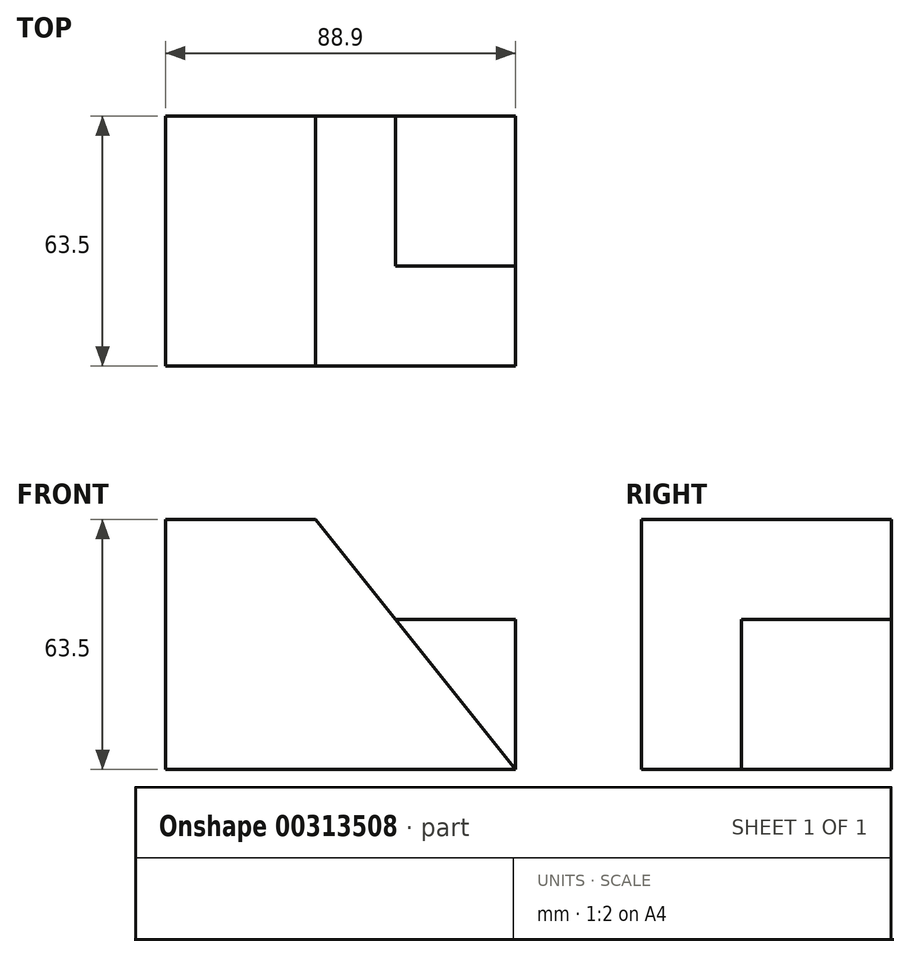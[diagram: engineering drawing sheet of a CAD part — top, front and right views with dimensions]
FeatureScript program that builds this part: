
annotation { "Feature Type Name" : "Feature", "Feature Type Description" : "" }
export const myFeature = defineFeature(function(context is Context, id is Id, definition is map)
    precondition{}
    {
        {
            var Q0;
            Q0=qCreatedBy(makeId("Front.planeOp"),FACE);
            var sketch = newSketch(context, id + "F0", { "sketchPlane" : qUnion([Q0])});
            skLineSegment(sketch, "E0", {"start": v(-58.27, -11.52) * mm, "end": v(30.63, -11.52) * mm});
            skLineSegment(sketch, "E1", {"start": v(-58.27, -11.52) * mm, "end": v(-58.27, 51.98) * mm});
            skLineSegment(sketch, "E2", {"start": v(-58.27, 51.98) * mm, "end": v(-20.17, 51.98) * mm});
            skLineSegment(sketch, "E3", {"start": v(-20.17, 51.98) * mm, "end": v(30.63, -11.52) * mm});
            skSolve(sketch);
        }
        {
            var Q0;
            Q0 = qSketchRegion(id + "F0", true);
            extrude(context, id + "F1", {"entities" : qUnion([Q0]), "depth" : 63.5 * mm});
        }
        {
            var Q0;
            Q0=makeQuery(id+"F1.opExtrude","CAP_FACE",FACE,{"disambiguationData":[OSD([sQuery(id+"F0.wireOp",EDGE,"E0"),sQuery(id+"F0.wireOp",EDGE,"E1"),sQuery(id+"F0.wireOp",EDGE,"E2"),sQuery(id+"F0.wireOp",EDGE,"E3")])],"isStart":true});
            var sketch = newSketch(context, id + "F2", { "sketchPlane" : qUnion([Q0])});
            skLineSegment(sketch, "E4", {"start": v(-30.63, -11.52) * mm, "end": v(-30.63, 26.58) * mm});
            skLineSegment(sketch, "E5", {"start": v(-30.63, 26.58) * mm, "end": v(-0.15, 26.58) * mm});
            skSolve(sketch);
        }
        {
            var Q0;
            Q0 = qSketchRegion(id + "F2", true);
            var Q1;
            {var subQ0=sQuery(id+"F2.wireOp",EDGE,"E4");Q1=makeQuery(id+"F2.imprint","IMPRINT",FACE,{"disambiguationData":[TD([[makeQuery(id+"F2.imprint","IMPRINT",EDGE,{"derivedFrom":subQ0}),-1.0]])]});}
            extrude(context, id + "F3", {"entities" : qUnion([Q0, Q1]), "operationType" : NewBodyOperationType.ADD, "oppositeDirection" : true, "depth" : 38.1 * mm});
        }
    });
